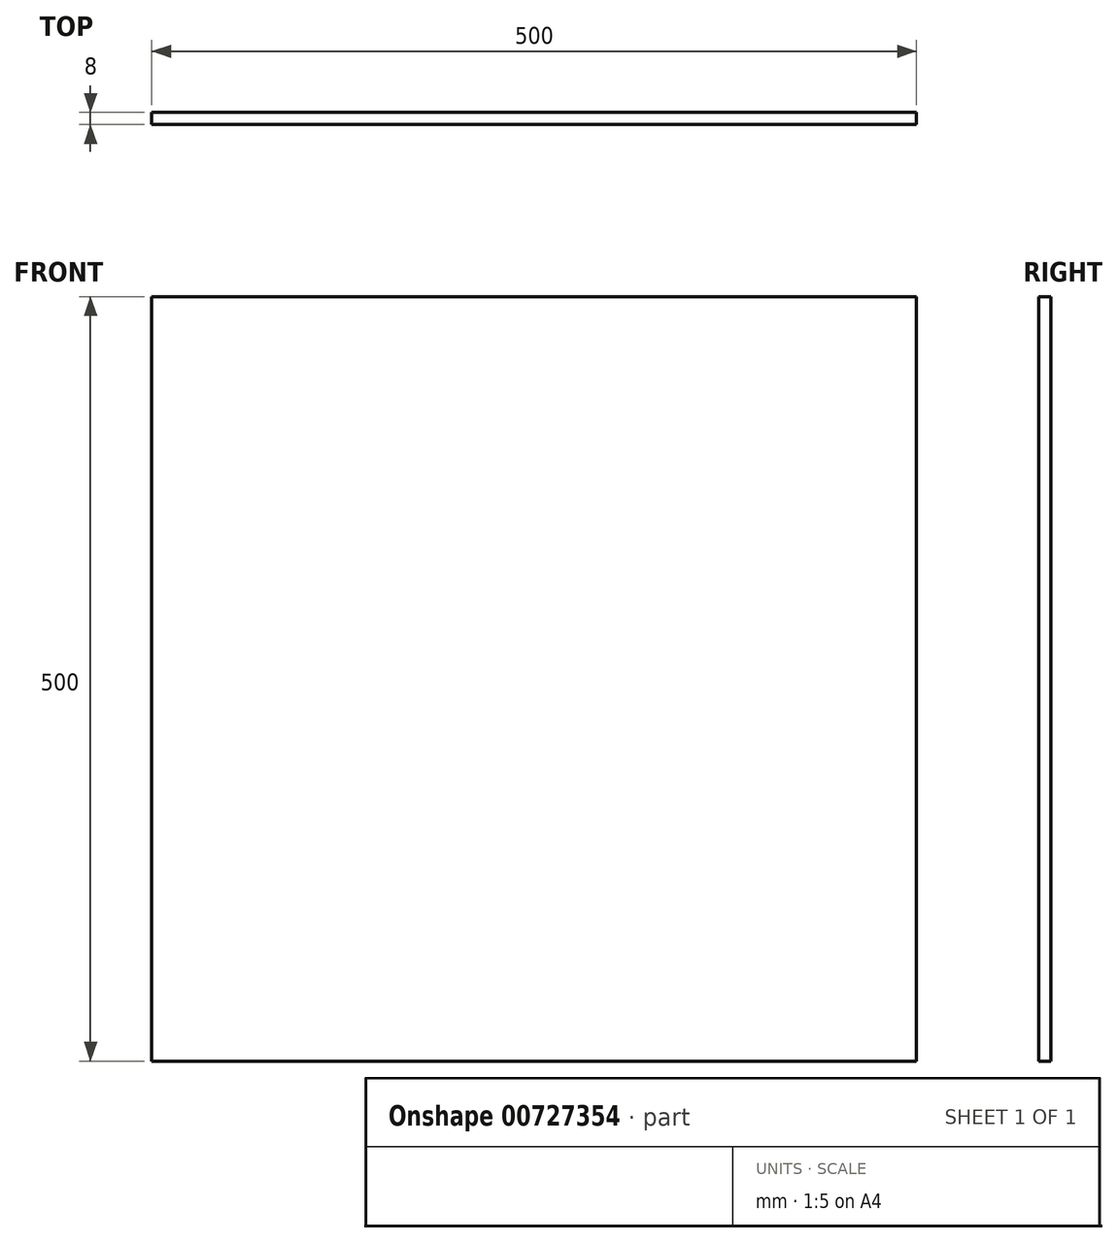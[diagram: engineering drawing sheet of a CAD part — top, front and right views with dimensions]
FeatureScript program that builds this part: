
annotation { "Feature Type Name" : "Feature", "Feature Type Description" : "" }
export const myFeature = defineFeature(function(context is Context, id is Id, definition is map)
    precondition{}
    {
        {
            var Q0;
            Q0=qCreatedBy(makeId("Front.planeOp"),FACE);
            var sketch = newSketch(context, id + "F0", { "sketchPlane" : qUnion([Q0])});
            skLineSegment(sketch, "E0.bottom", {"start": v(0, 0) * mm, "end": v(500, 0) * mm});
            skLineSegment(sketch, "E0.top", {"start": v(0, 500) * mm, "end": v(500, 500) * mm});
            skLineSegment(sketch, "E0.left", {"start": v(0, 0) * mm, "end": v(0, 500) * mm});
            skLineSegment(sketch, "E0.right", {"start": v(500, 0) * mm, "end": v(500, 500) * mm});
            skSolve(sketch);
        }
        {
            var Q0;
            Q0=makeQuery(id+"F0.imprint","IMPRINT",FACE,{"disambiguationData":[TD([[makeQuery(id+"F0.imprint","IMPRINT",EDGE,{"derivedFrom":sQuery(id+"F0.wireOp",EDGE,"E0.bottom")}),1.0]])]});
            extrude(context, id + "F1", {"entities" : qUnion([Q0]), "depth" : 8 * mm, "offsetDistance" : 25 * mm});
        }
    });
